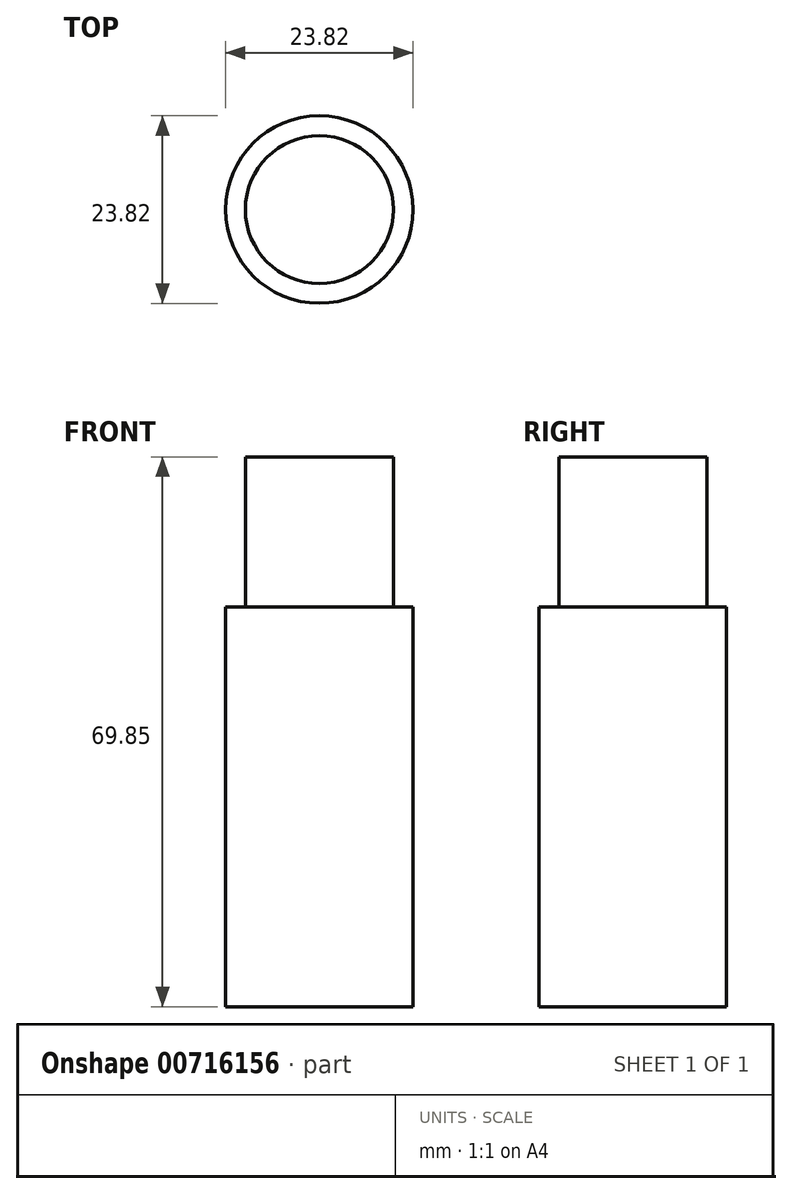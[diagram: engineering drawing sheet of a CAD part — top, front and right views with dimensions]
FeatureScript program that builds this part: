
annotation { "Feature Type Name" : "Feature", "Feature Type Description" : "" }
export const myFeature = defineFeature(function(context is Context, id is Id, definition is map)
    precondition{}
    {
        {
            var Q0;
            Q0=qCreatedBy(makeId("Top.planeOp"),FACE);
            var sketch = newSketch(context, id + "F0", { "sketchPlane" : qUnion([Q0])});
            skCircle(sketch, "E0", {"center": v(0, 0) * mm, "radius": 11.9 * mm});
            skSolve(sketch);
        }
        {
            var Q0;
            Q0 = qSketchRegion(id + "F0", true);
            extrude(context, id + "F1", {"entities" : qUnion([Q0]), "endBound" : BoundingType.SYMMETRIC, "oppositeDirection" : true, "depth" : 50.8 * mm, "offsetDistance" : 25.4 * mm});
        }
        {
            var Q0;
            Q0=makeQuery(id+"F1.opExtrude","CAP_FACE",FACE,{"disambiguationData":[OSD([sQuery(id+"F0.wireOp",EDGE,"E0")])],"isStart":true});
            var sketch = newSketch(context, id + "F2", { "sketchPlane" : qUnion([Q0])});
            skCircle(sketch, "E1", {"center": v(0, 0) * mm, "radius": 9.4 * mm});
            skSolve(sketch);
        }
        {
            var Q0;
            Q0 = qSketchRegion(id + "F2", true);
            extrude(context, id + "F3", {"entities" : qUnion([Q0]), "operationType" : NewBodyOperationType.ADD, "depth" : 19.05 * mm, "offsetDistance" : 25.4 * mm});
        }
    });
